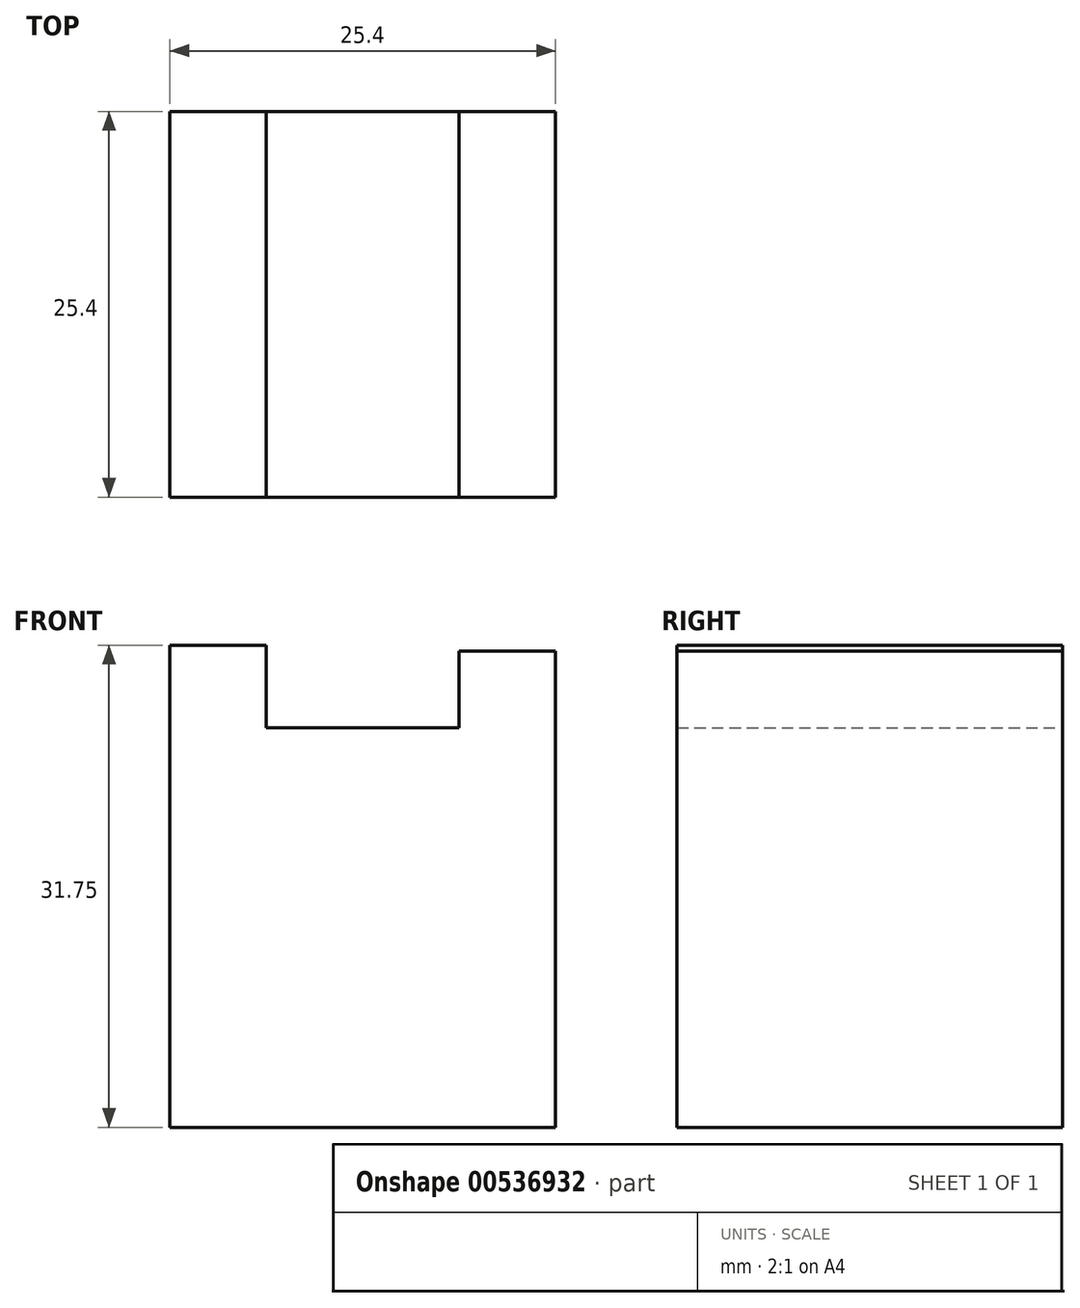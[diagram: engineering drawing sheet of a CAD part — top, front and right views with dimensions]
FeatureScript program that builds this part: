
annotation { "Feature Type Name" : "Feature", "Feature Type Description" : "" }
export const myFeature = defineFeature(function(context is Context, id is Id, definition is map)
    precondition{}
    {
        {
            var Q0;
            Q0=qCreatedBy(makeId("Front.planeOp"),FACE);
            var sketch = newSketch(context, id + "F0", { "sketchPlane" : qUnion([Q0])});
            skLineSegment(sketch, "E0", {"start": v(-33.75, 0) * mm, "end": v(-33.75, 31.75) * mm});
            skLineSegment(sketch, "E1", {"start": v(-33.75, 31.75) * mm, "end": v(-27.4, 31.75) * mm});
            skLineSegment(sketch, "E2", {"start": v(-27.4, 31.75) * mm, "end": v(-27.4, 26.32) * mm});
            skLineSegment(sketch, "E3", {"start": v(-27.4, 26.32) * mm, "end": v(-14.7, 26.32) * mm});
            skLineSegment(sketch, "E4", {"start": v(-14.7, 26.32) * mm, "end": v(-14.7, 31.36) * mm});
            skLineSegment(sketch, "E5", {"start": v(-14.7, 31.36) * mm, "end": v(-8.35, 31.36) * mm});
            skLineSegment(sketch, "E6", {"start": v(-8.35, 31.36) * mm, "end": v(-8.35, 0) * mm});
            skLineSegment(sketch, "E7", {"start": v(-8.35, 0) * mm, "end": v(-33.75, 0) * mm});
            skSolve(sketch);
        }
        {
            var Q0;
            Q0 = qSketchRegion(id + "F0", true);
            extrude(context, id + "F1", {"entities" : qUnion([Q0]), "depth" : 25.4 * mm, "offsetDistance" : 25.4 * mm});
        }
    });
